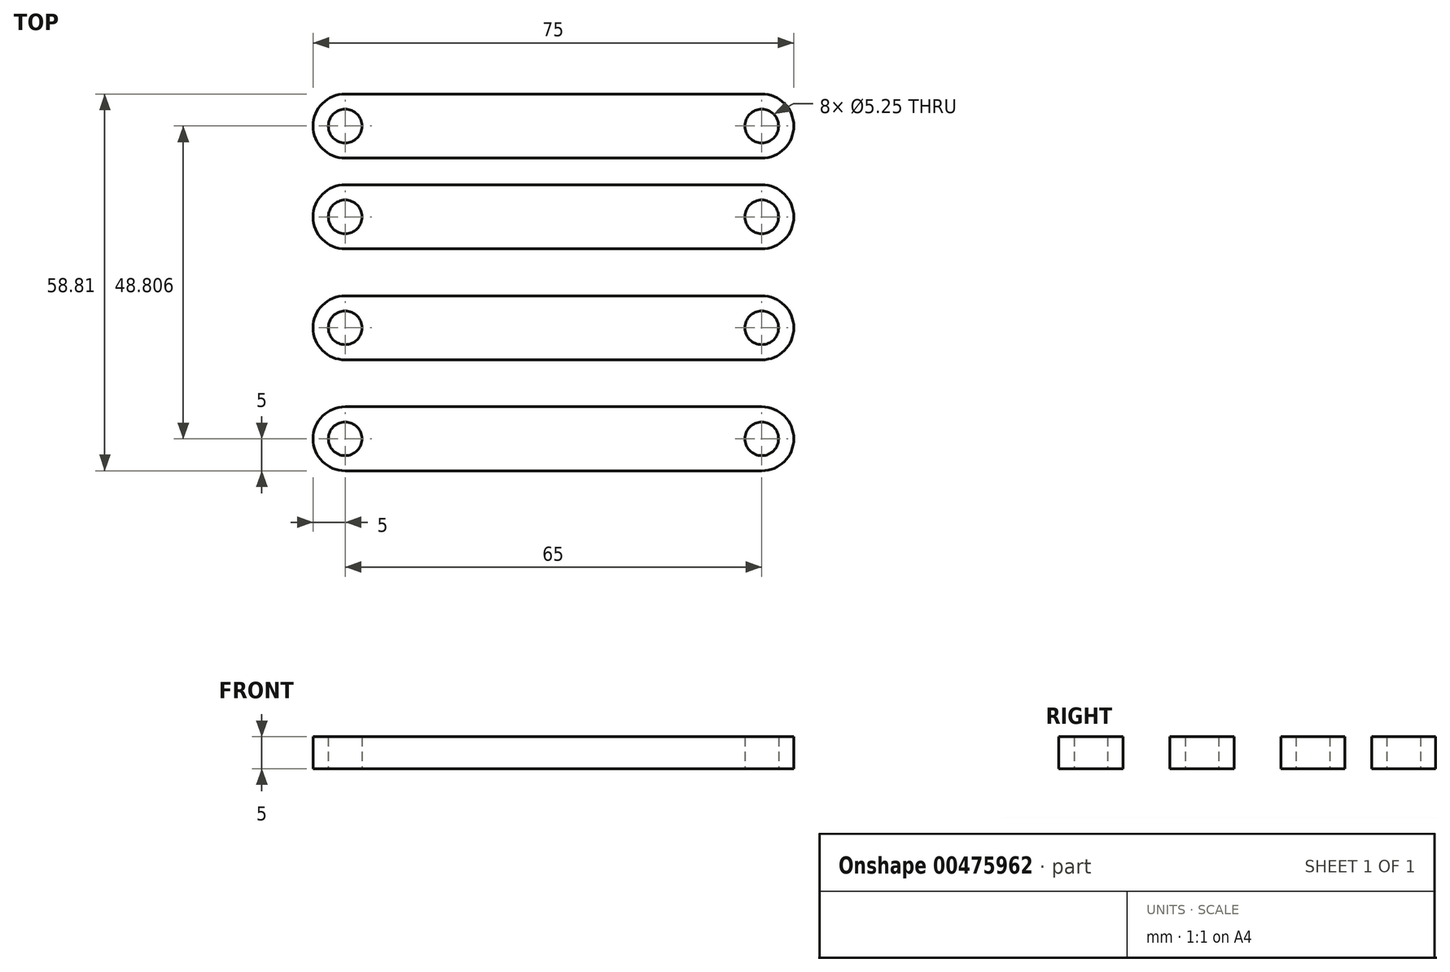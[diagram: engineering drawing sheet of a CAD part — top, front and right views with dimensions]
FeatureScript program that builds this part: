
annotation { "Feature Type Name" : "Feature", "Feature Type Description" : "" }
export const myFeature = defineFeature(function(context is Context, id is Id, definition is map)
    precondition{}
    {
        {
            var Q0;
            Q0=qCreatedBy(makeId("Top.planeOp"),FACE);
            var sketch = newSketch(context, id + "F0", { "sketchPlane" : qUnion([Q0])});
            skLineSegment(sketch, "E0.bottom", {"start": v(-54.14, 40.23) * mm, "end": v(10.86, 40.23) * mm});
            skLineSegment(sketch, "E0.top", {"start": v(-54.14, 30.23) * mm, "end": v(10.86, 30.23) * mm});
            skLineSegment(sketch, "E0.left", {"start": v(-54.14, 40.23) * mm, "end": v(-54.14, 30.23) * mm});
            skLineSegment(sketch, "E0.right", {"start": v(10.86, 40.23) * mm, "end": v(10.86, 30.23) * mm});
            skLineSegment(sketch, "E1.bottom", {"start": v(-54.14, 26.06) * mm, "end": v(10.86, 26.06) * mm});
            skLineSegment(sketch, "E1.top", {"start": v(-54.14, 16.06) * mm, "end": v(10.86, 16.06) * mm});
            skLineSegment(sketch, "E1.left", {"start": v(-54.14, 26.06) * mm, "end": v(-54.14, 16.06) * mm});
            skLineSegment(sketch, "E1.right", {"start": v(10.86, 26.06) * mm, "end": v(10.86, 16.06) * mm});
            skLineSegment(sketch, "E2.bottom", {"start": v(-54.14, 8.74) * mm, "end": v(10.86, 8.74) * mm});
            skLineSegment(sketch, "E2.top", {"start": v(-54.14, -1.26) * mm, "end": v(10.86, -1.26) * mm});
            skLineSegment(sketch, "E2.left", {"start": v(-54.14, 8.74) * mm, "end": v(-54.14, -1.26) * mm});
            skLineSegment(sketch, "E2.right", {"start": v(10.86, 8.74) * mm, "end": v(10.86, -1.26) * mm});
            skLineSegment(sketch, "E3.bottom", {"start": v(-54.14, -8.58) * mm, "end": v(10.86, -8.58) * mm});
            skLineSegment(sketch, "E3.top", {"start": v(-54.14, -18.58) * mm, "end": v(10.86, -18.58) * mm});
            skLineSegment(sketch, "E3.left", {"start": v(-54.14, -8.58) * mm, "end": v(-54.14, -18.58) * mm});
            skLineSegment(sketch, "E3.right", {"start": v(10.86, -8.58) * mm, "end": v(10.86, -18.58) * mm});
            skArc(sketch, "E4", {"start": v(-54.14, 40.23) * mm, "mid": v(-59.14, 35.23) * mm, "end": v(-54.14, 30.23) * mm});
            skArc(sketch, "E5", {"start": v(10.86, 30.23) * mm, "mid": v(15.86, 35.23) * mm, "end": v(10.86, 40.23) * mm});
            skArc(sketch, "E6", {"start": v(10.86, 16.06) * mm, "mid": v(15.86, 21.06) * mm, "end": v(10.86, 26.06) * mm});
            skArc(sketch, "E7", {"start": v(-54.14, 26.06) * mm, "mid": v(-59.14, 21.06) * mm, "end": v(-54.14, 16.06) * mm});
            skArc(sketch, "E8", {"start": v(-54.14, 8.74) * mm, "mid": v(-59.14, 3.74) * mm, "end": v(-54.14, -1.26) * mm});
            skArc(sketch, "E9", {"start": v(-54.14, -8.58) * mm, "mid": v(-59.14, -13.58) * mm, "end": v(-54.14, -18.58) * mm});
            skArc(sketch, "E10", {"start": v(10.86, -18.58) * mm, "mid": v(15.86, -13.58) * mm, "end": v(10.86, -8.58) * mm});
            skArc(sketch, "E11", {"start": v(10.86, -1.26) * mm, "mid": v(15.86, 3.74) * mm, "end": v(10.86, 8.74) * mm});
            skCircle(sketch, "E12", {"center": v(-54.14, 35.23) * mm, "radius": 2.62 * mm});
            skCircle(sketch, "E13", {"center": v(10.86, 35.23) * mm, "radius": 2.62 * mm});
            skCircle(sketch, "E14", {"center": v(10.86, 21.06) * mm, "radius": 2.62 * mm});
            skCircle(sketch, "E15", {"center": v(-54.14, 21.06) * mm, "radius": 2.62 * mm});
            skCircle(sketch, "E16", {"center": v(-54.14, 3.74) * mm, "radius": 2.62 * mm});
            skCircle(sketch, "E17", {"center": v(10.86, 3.74) * mm, "radius": 2.62 * mm});
            skCircle(sketch, "E18", {"center": v(10.86, -13.58) * mm, "radius": 2.62 * mm});
            skCircle(sketch, "E19", {"center": v(-54.14, -13.58) * mm, "radius": 2.62 * mm});
            skSolve(sketch);
        }
        {
            var Q0;
            Q0 = qSketchRegion(id + "F0", true);
            extrude(context, id + "F1", {"entities" : qUnion([Q0]), "depth" : 5 * mm});
        }
    });
